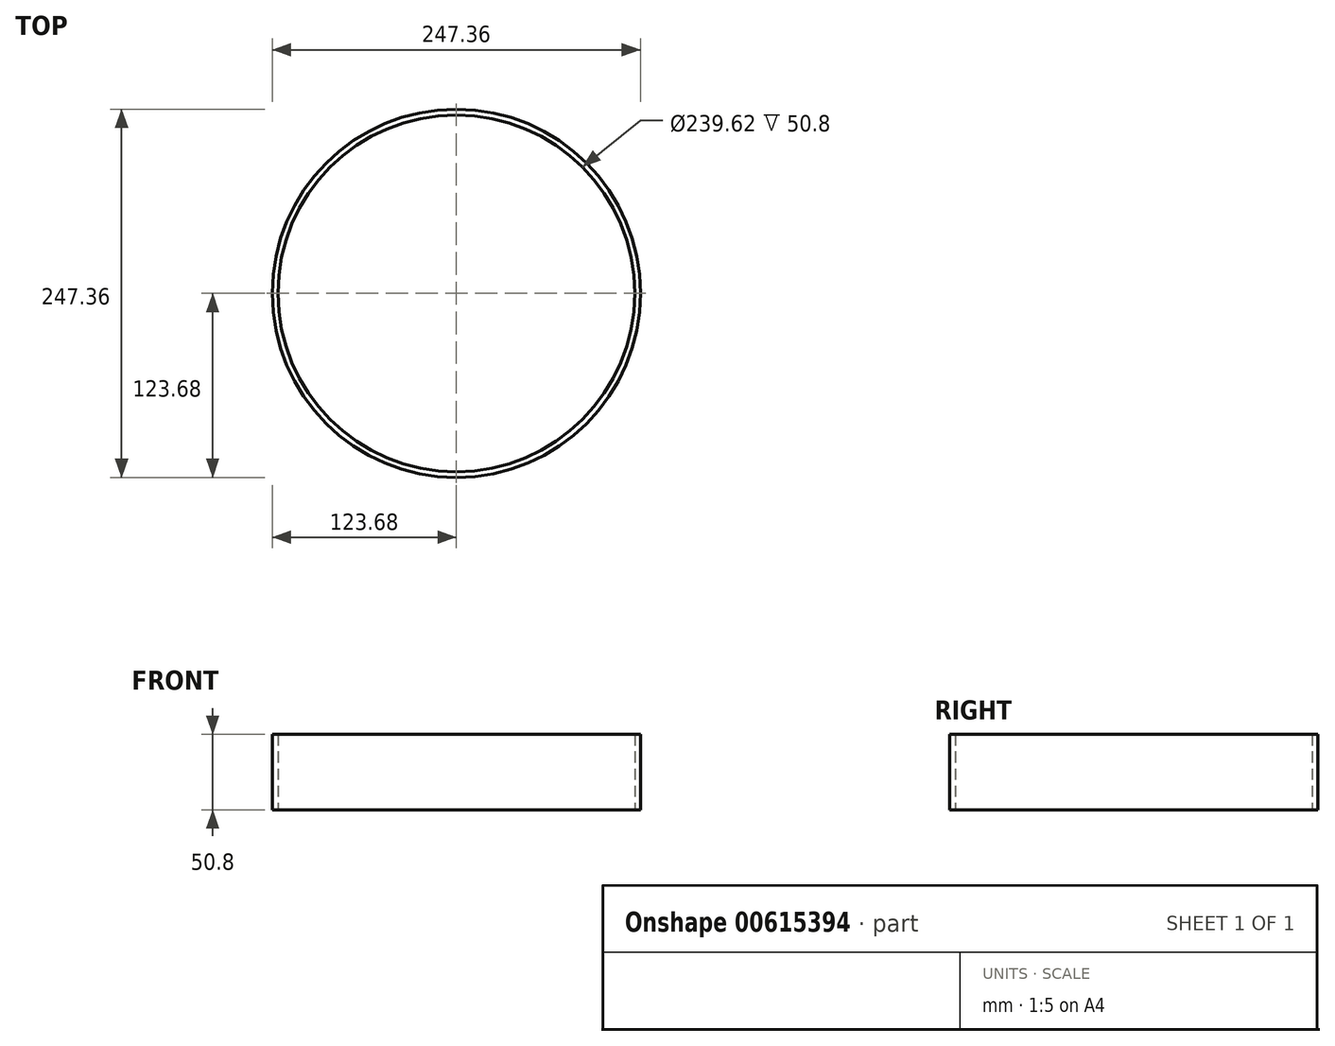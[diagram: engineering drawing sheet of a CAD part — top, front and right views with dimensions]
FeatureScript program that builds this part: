
annotation { "Feature Type Name" : "Feature", "Feature Type Description" : "" }
export const myFeature = defineFeature(function(context is Context, id is Id, definition is map)
    precondition{}
    {
        {
            var Q0;
            Q0=qCreatedBy(makeId("Top.planeOp"),FACE);
            var sketch = newSketch(context, id + "F0", { "sketchPlane" : qUnion([Q0])});
            skCircle(sketch, "E0", {"center": v(0, 0) * mm, "radius": 123.68 * mm});
            skCircle(sketch, "E1", {"center": v(0, 0) * mm, "radius": 119.81 * mm});
            skSolve(sketch);
        }
        {
            var Q0;
            Q0 = qSketchRegion(id + "F0", true);
            extrude(context, id + "F1", {"entities" : qUnion([Q0]), "depth" : 50.8 * mm, "offsetDistance" : 25.4 * mm});
        }
    });
